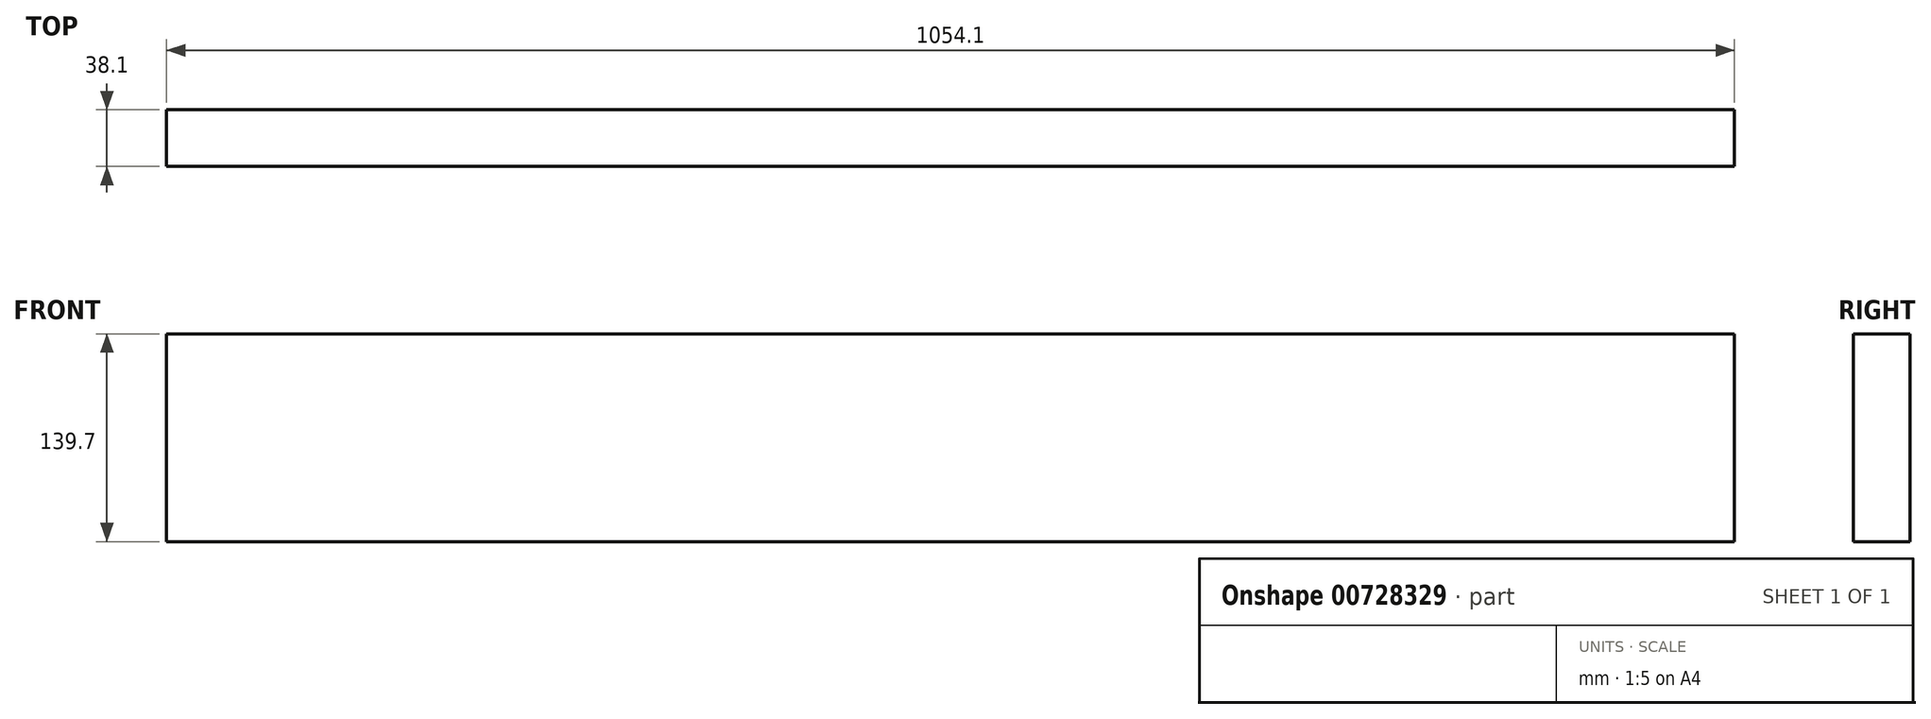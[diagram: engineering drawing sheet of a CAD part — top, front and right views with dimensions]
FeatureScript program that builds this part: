
annotation { "Feature Type Name" : "Feature", "Feature Type Description" : "" }
export const myFeature = defineFeature(function(context is Context, id is Id, definition is map)
    precondition{}
    {
        {
            var Q0;
            Q0=qCreatedBy(makeId("Front.planeOp"),FACE);
            var sketch = newSketch(context, id + "F0", { "sketchPlane" : qUnion([Q0])});
            skLineSegment(sketch, "E0.bottom", {"start": v(-527.05, -69.85) * mm, "end": v(527.05, -69.85) * mm});
            skLineSegment(sketch, "E0.top", {"start": v(-527.05, 69.85) * mm, "end": v(527.05, 69.85) * mm});
            skLineSegment(sketch, "E0.left", {"start": v(-527.05, -69.85) * mm, "end": v(-527.05, 69.85) * mm});
            skLineSegment(sketch, "E0.right", {"start": v(527.05, -69.85) * mm, "end": v(527.05, 69.85) * mm});
            skPoint(sketch, "E0.middle", {"position": v(0, 0) * mm});
            skSolve(sketch);
        }
        {
            var Q0;
            Q0=qSketchRegion(id+"F0",true);
            extrude(context, id + "F1", {"entities" : qUnion([Q0]), "depth" : 38.1 * mm});
        }
    });
